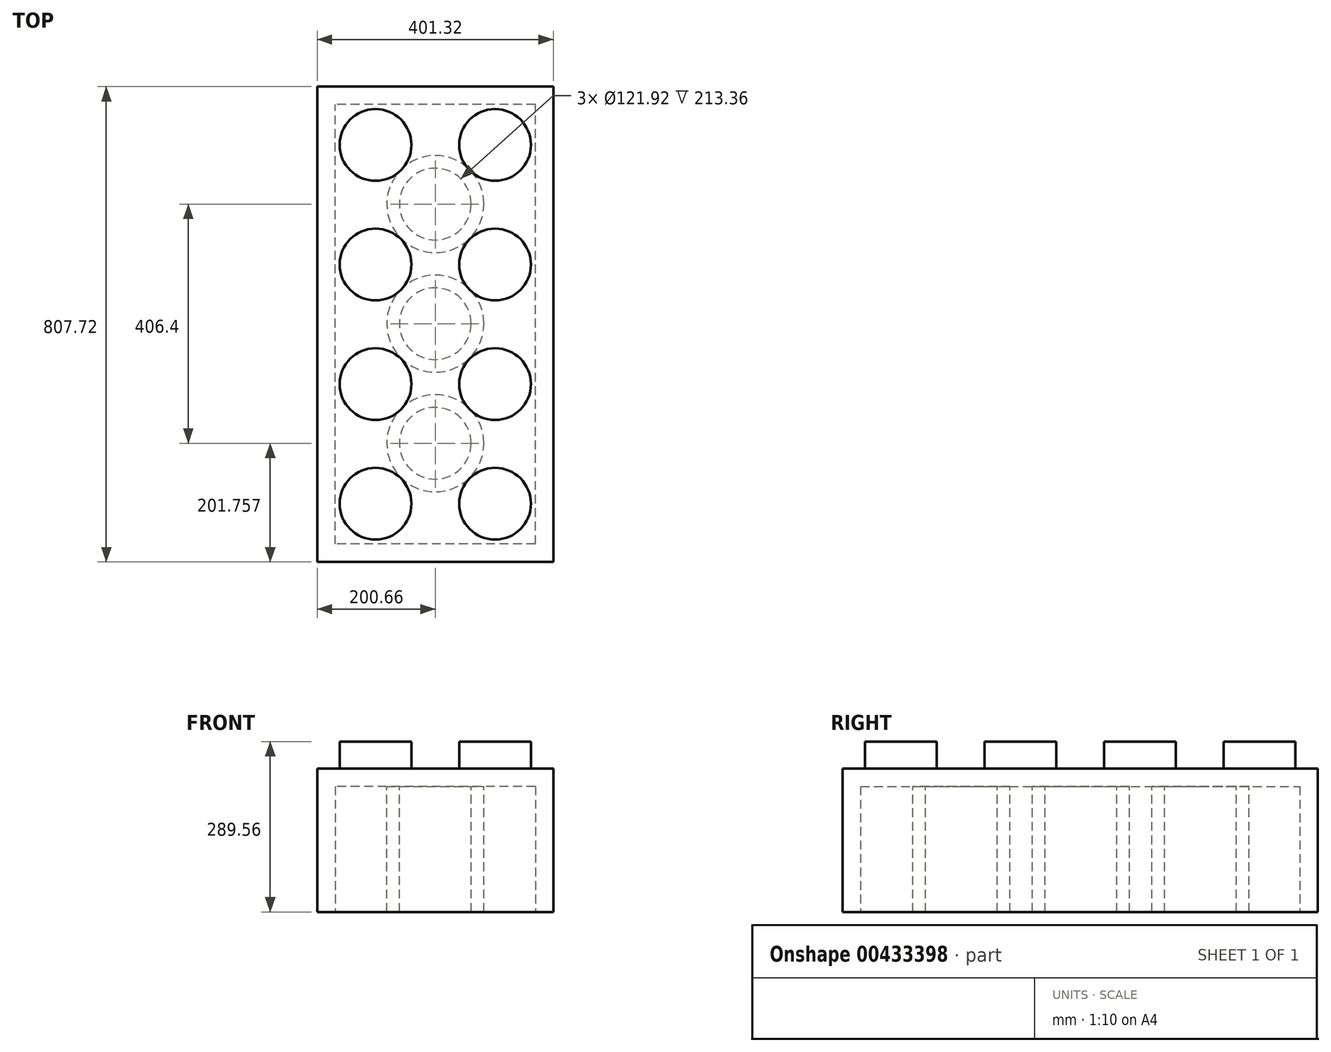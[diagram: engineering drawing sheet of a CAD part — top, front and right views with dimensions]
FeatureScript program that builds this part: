
annotation { "Feature Type Name" : "Feature", "Feature Type Description" : "" }
export const myFeature = defineFeature(function(context is Context, id is Id, definition is map)
    precondition{}
    {
        {
            var Q0;
            Q0=qCreatedBy(makeId("Front.planeOp"),FACE);
            var sketch = newSketch(context, id + "F0", { "sketchPlane" : qUnion([Q0])});
            skLineSegment(sketch, "E0.bottom", {"start": v(-200.66, 121.92) * mm, "end": v(200.66, 121.92) * mm});
            skLineSegment(sketch, "E0.top", {"start": v(-200.66, -121.92) * mm, "end": v(200.66, -121.92) * mm});
            skLineSegment(sketch, "E0.left", {"start": v(-200.66, 121.92) * mm, "end": v(-200.66, -121.92) * mm});
            skLineSegment(sketch, "E0.right", {"start": v(200.66, 121.92) * mm, "end": v(200.66, -121.92) * mm});
            skPoint(sketch, "E0.middle", {"position": v(0, 0) * mm});
            skSolve(sketch);
        }
        {
            var Q0;
            Q0=makeQuery(id+"F0.imprint","IMPRINT",FACE,{"disambiguationData":[TD([[makeQuery(id+"F0.imprint","IMPRINT",EDGE,{"derivedFrom":sQuery(id+"F0.wireOp",EDGE,"E0.bottom")}),-1.0]])]});
            extrude(context, id + "F1", {"entities" : qUnion([Q0]), "depth" : 807.72 * mm});
        }
        {
            var Q0;
            Q0=makeQuery(id+"F1.opExtrude","SWEPT_FACE",FACE,{"disambiguationData":[OSD([sQuery(id+"F0.wireOp",EDGE,"E0.bottom")])]});
            var sketch = newSketch(context, id + "F2", { "sketchPlane" : qUnion([Q0])});
            skCircle(sketch, "E1", {"center": v(-101.6, -708.66) * mm, "radius": 60.96 * mm});
            skCircle(sketch, "E2.0.1.0", {"center": v(-101.6, -505.46) * mm, "radius": 60.96 * mm});
            skCircle(sketch, "E2.0.2.0", {"center": v(-101.6, -302.26) * mm, "radius": 60.96 * mm});
            skCircle(sketch, "E2.0.3.0", {"center": v(-101.6, -99.06) * mm, "radius": 60.96 * mm});
            skCircle(sketch, "E2.1.0.0", {"center": v(101.6, -708.66) * mm, "radius": 60.96 * mm});
            skCircle(sketch, "E2.1.1.0", {"center": v(101.6, -505.46) * mm, "radius": 60.96 * mm});
            skCircle(sketch, "E2.1.2.0", {"center": v(101.6, -302.26) * mm, "radius": 60.96 * mm});
            skCircle(sketch, "E2.1.3.0", {"center": v(101.6, -99.06) * mm, "radius": 60.96 * mm});
            skLineSegment(sketch, "E2.direction1", {"start": v(-101.6, -708.66) * mm, "end": v(101.6, -708.66) * mm, "construction": true});
            skLineSegment(sketch, "E2.direction2", {"start": v(-101.6, -708.66) * mm, "end": v(-101.6, -505.46) * mm, "construction": true});
            skSolve(sketch);
        }
        {
            var Q0;
            Q0 = qSketchRegion(id + "F2", true);
            extrude(context, id + "F3", {"entities" : qUnion([Q0]), "operationType" : NewBodyOperationType.ADD, "depth" : 45.72 * mm});
        }
        {
            var Q0;
            Q0=makeQuery(id+"F1.opExtrude","SWEPT_FACE",FACE,{"disambiguationData":[OSD([sQuery(id+"F0.wireOp",EDGE,"E0.top")])]});
            var sketch = newSketch(context, id + "F4", { "sketchPlane" : qUnion([Q0])});
            skLineSegment(sketch, "E3.bottom", {"start": v(170.18, 777.24) * mm, "end": v(-170.18, 777.24) * mm});
            skLineSegment(sketch, "E3.top", {"start": v(170.18, 30.48) * mm, "end": v(-170.18, 30.48) * mm});
            skLineSegment(sketch, "E3.left", {"start": v(170.18, 777.24) * mm, "end": v(170.18, 30.48) * mm});
            skLineSegment(sketch, "E3.right", {"start": v(-170.18, 777.24) * mm, "end": v(-170.18, 30.48) * mm});
            skSolve(sketch);
        }
        {
            var Q0;
            Q0=makeQuery(id+"F4.imprint","IMPRINT",FACE,{"disambiguationData":[TD([[makeQuery(id+"F4.imprint","IMPRINT",EDGE,{"derivedFrom":sQuery(id+"F4.wireOp",EDGE,"E3.bottom")}),1.0]])]});
            extrude(context, id + "F5", {"entities" : qUnion([Q0]), "operationType" : NewBodyOperationType.REMOVE, "oppositeDirection" : true, "depth" : 213.36 * mm});
        }
        {
            var Q0;
            Q0=makeQuery(id+"F5.boolean.opBoolean","COPY",FACE,{"derivedFrom":makeQuery(id+"F5.opExtrude","CAP_FACE",FACE,{"disambiguationData":[OSD([sQuery(id+"F4.wireOp",EDGE,"E3.bottom"),sQuery(id+"F4.wireOp",EDGE,"E3.top"),sQuery(id+"F4.wireOp",EDGE,"E3.left"),sQuery(id+"F4.wireOp",EDGE,"E3.right")])],"isStart":false})});
            var sketch = newSketch(context, id + "F6", { "sketchPlane" : qUnion([Q0])});
            skCircle(sketch, "E4", {"center": v(0, 605.96) * mm, "radius": 82.55 * mm});
            skCircle(sketch, "E5", {"center": v(0, 605.96) * mm, "radius": 60.96 * mm});
            skCircle(sketch, "E6.0.1.0", {"center": v(0, 402.76) * mm, "radius": 82.55 * mm});
            skCircle(sketch, "E6.0.1.1", {"center": v(0, 402.76) * mm, "radius": 60.96 * mm});
            skCircle(sketch, "E6.0.2.0", {"center": v(0, 199.56) * mm, "radius": 82.55 * mm});
            skCircle(sketch, "E6.0.2.1", {"center": v(0, 199.56) * mm, "radius": 60.96 * mm});
            skLineSegment(sketch, "E6.direction1", {"start": v(0, 605.96) * mm, "end": v(25.4, 605.96) * mm, "construction": true});
            skLineSegment(sketch, "E6.direction2", {"start": v(0, 605.96) * mm, "end": v(0, 402.76) * mm, "construction": true});
            skSolve(sketch);
        }
        {
            var Q0;
            Q0=makeQuery(id+"F6.imprint","IMPRINT",FACE,{"disambiguationData":[TD([[makeQuery(id+"F6.imprint","IMPRINT",EDGE,{"derivedFrom":sQuery(id+"F6.wireOp",EDGE,"E4")}),1.0]])]});
            var Q1;
            Q1=makeQuery(id+"F6.imprint","IMPRINT",FACE,{"disambiguationData":[TD([[makeQuery(id+"F6.imprint","IMPRINT",EDGE,{"derivedFrom":sQuery(id+"F6.wireOp",EDGE,"E6.0.1.0")}),1.0]])]});
            var Q2;
            Q2=makeQuery(id+"F6.imprint","IMPRINT",FACE,{"disambiguationData":[TD([[makeQuery(id+"F6.imprint","IMPRINT",EDGE,{"derivedFrom":sQuery(id+"F6.wireOp",EDGE,"E6.0.2.0")}),1.0]])]});
            extrude(context, id + "F7", {"entities" : qUnion([Q0, Q1, Q2]), "operationType" : NewBodyOperationType.ADD, "depth" : 213.36 * mm});
        }
    });
